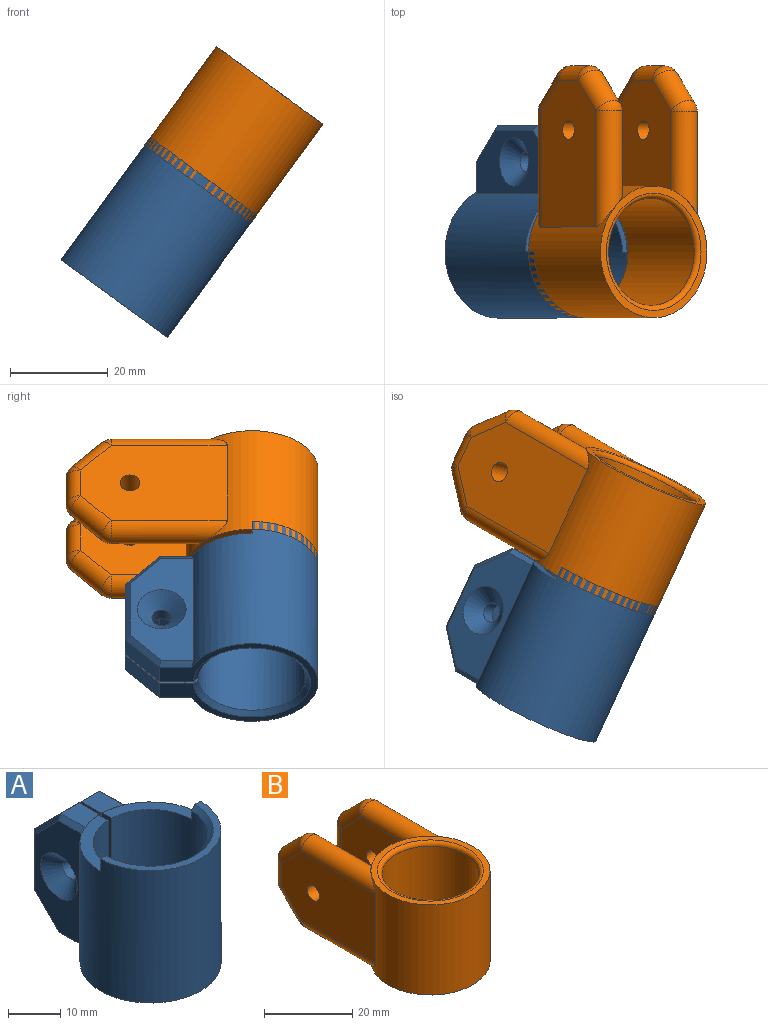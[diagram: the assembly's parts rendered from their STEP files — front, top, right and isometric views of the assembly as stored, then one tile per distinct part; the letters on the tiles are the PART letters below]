
ASSEMBLY  parts=2 mates=1
PART A: 44 faces, bbox 27x39.5x31 mm
  f0: plane 32.5x27mm, normal (0,0,-1), area 177.2mm2, adj f2,f4,f9,f12,f13,f23,f28,f33
  f1: plane 6.56x5mm, normal (0,0,1), area 29.3mm2, adj f2,f4,f14,f27,f36,f37
  f2: plane 28x12.27mm, normal (-1,0,0), area 252mm2, adj f0,f1,f11,f13,f14,f17,f18,f19
  f3: plane 26x13.03mm, normal (1,0,0), area 255.2mm2, adj f4,f17,f18,f19,f20,f21,f22,f23
  f4: cylinder r=13.5mm len=31mm, axis (0,0,-1), area 2141.3mm2, adj f0,f1,f3,f6,f8,f10,f23,f27
  f5: cylinder r=11mm len=29mm, axis (0,0,-1), area 1908.8mm2, adj f33,f34,f36,f39,f40,f41,f42,f43
  f6: plane 27x13.5mm, normal (0,0,1), area 60.1mm2, adj f4,f34,f41,f42
  f7: plane 14x5mm, normal (0,1,0), area 70mm2, adj f9,f12,f15,f30
  f8: plane 6.56x5mm, normal (0,0,1), area 29.3mm2, adj f4,f9,f15,f32,f38,f39
  f9: plane 28x12.27mm, normal (1,0,0), area 281.9mm2, adj f0,f7,f8,f12,f15,f16,f38
  f10: plane 26x13.03mm, normal (-1,0,0), area 219.1mm2, adj f4,f28,f29,f30,f31,f32,f35
  f11: plane 14x5mm, normal (0,1,0), area 70mm2, adj f2,f13,f14,f25
  f12: plane 7x7mm, normal (0,0.71,-0.71), area 49.5mm2, adj f0,f7,f9,f29
  f13: plane 7x7mm, normal (0,0.71,-0.71), area 49.5mm2, adj f0,f2,f11,f24
  f14: plane 7x7mm, normal (0,0.71,0.71), area 49.5mm2, adj f1,f2,f11,f26
  f15: plane 7x7mm, normal (0,0.71,0.71), area 49.5mm2, adj f7,f8,f9,f31
  f16: cylinder r=2mm len=4mm, axis (1,0,0), area 37.7mm2, adj f9,f35
  f17: plane 6x4.01mm, normal (0,-0.99,0.13), area 24.2mm2, adj f2,f3,f18,f22
  f18: plane 6x3.73mm, normal (0,-0.39,0.92), area 24.2mm2, adj f2,f3,f17,f19
  f19: plane 6x3.22mm, normal (0,0.61,0.8), area 24.2mm2, adj f2,f3,f18,f20
  f20: plane 6x4.01mm, normal (0,0.99,-0.13), area 24.2mm2, adj f2,f3,f19,f21
  f21: plane 6x3.73mm, normal (0,0.39,-0.92), area 24.2mm2, adj f2,f3,f20,f22
  f22: plane 6x3.22mm, normal (0,-0.61,-0.8), area 24.2mm2, adj f2,f3,f17,f21
  f23: plane 7.04x1.01mm, normal (0.71,0,-0.71), area 9.3mm2, adj f0,f3,f4,f24
  f24: plane 7.41x7.41mm, normal (0.71,0.5,-0.5), area 13.4mm2, adj f3,f13,f23,f25
  f25: plane 14x1mm, normal (0.71,0.71,0), area 19.2mm2, adj f3,f11,f24,f26
  f26: plane 7.41x7.41mm, normal (0.71,0.5,0.5), area 13.4mm2, adj f3,f14,f25,f27
  f27: plane 7.04x1.01mm, normal (0.71,0,0.71), area 9.3mm2, adj f1,f3,f4,f26
  f28: plane 7.04x1.01mm, normal (-0.71,0,-0.71), area 9.3mm2, adj f0,f4,f10,f29
  f29: plane 7.41x7.41mm, normal (-0.71,0.5,-0.5), area 13.4mm2, adj f10,f12,f28,f30
  f30: plane 14x1mm, normal (-0.71,0.71,0), area 19.2mm2, adj f7,f10,f29,f31
  f31: plane 7.41x7.41mm, normal (-0.71,0.5,0.5), area 13.4mm2, adj f10,f15,f30,f32
  f32: plane 7.04x1.01mm, normal (-0.71,0,0.71), area 9.3mm2, adj f4,f8,f10,f31
  f33: cone r=12mm half-angle=45deg, axis (0,0,-1), area 100.8mm2, adj f0,f5,f36,f39
  f34: cone r=11mm half-angle=45deg, axis (0,0,1), area 51.1mm2, adj f5,f6,f41,f42
  f35: cone r=5mm half-angle=45deg, axis (-1,0,0), area 93.3mm2, adj f10,f16
  f36: plane 28.02x2.75mm, normal (-1,0,0), area 76.4mm2, adj f0,f1,f4,f5,f33,f37,f43
  f37: plane 28x0.25mm, normal (0,-1,0), area 6.9mm2, adj f0,f1,f2,f36
  f38: plane 28x0.25mm, normal (0,-1,0), area 7.1mm2, adj f0,f8,f9,f39
  f39: plane 28.02x2.75mm, normal (1,0,0), area 76.4mm2, adj f0,f4,f5,f8,f33,f38,f40
  f40: plane 13.49x13mm, normal (0,0,1), area 46.8mm2, adj f4,f5,f39,f41
  f41: plane 2.98x2.5mm, normal (0,1,0), area 7mm2, adj f4,f5,f6,f34,f40
  f42: plane 2.98x2.5mm, normal (0,1,0), area 7mm2, adj f4,f5,f6,f34,f43
  f43: plane 13.49x13mm, normal (0,0,1), area 46.9mm2, adj f4,f5,f36,f42
PART B: 31 faces, bbox 27.5x51.9x25 mm
  f0: plane 23.27x19mm, normal (-1,0,0), area 390.5mm2, adj f1,f9,f20,f22,f24,f26,f27
  f1: cylinder r=13.5mm len=25mm, axis (0,0,-1), area 348.2mm2, adj f0,f2,f7,f8,f11,f18,f20,f27
  f2: plane 23.27x19mm, normal (1,0,0), area 390.5mm2, adj f1,f10,f11,f13,f15,f17,f18
  f3: plane 30x19mm, normal (-1,0,0), area 518.5mm2, adj f4,f10,f11,f13,f15,f17,f18
  f4: cylinder r=13.5mm len=27mm, axis (0,0,-1), area 1338.4mm2, adj f3,f5,f7,f8,f11,f18,f20,f27
  f5: plane 30x19mm, normal (1,0,0), area 518.5mm2, adj f4,f9,f20,f22,f24,f26,f27
  f6: cylinder r=11mm len=23mm, axis (0,0,-1), area 1589.6mm2, adj f29,f30
  f7: plane 27x27mm, normal (0,0,1), area 120.2mm2, adj f1,f4,f30
  f8: plane 27x27mm, normal (0,0,-1), area 120.2mm2, adj f1,f4,f29
  f9: cylinder r=2mm len=6mm, axis (1,0,0), area 75.4mm2, adj f0,f5
  f10: cylinder r=2mm len=6mm, axis (1,0,0), area 75.4mm2, adj f2,f3
  f11: cylinder r=3mm len=23.76mm, axis (0,1,0), area 186.6mm2, adj f1,f2,f3,f4,f12
  f12: sphere r=3mm, area 14.1mm2, adj f11,f13
  f13: cylinder r=3mm len=8.36mm, axis (0,0.71,0.71), area 83.2mm2, adj f2,f3,f12,f14
  f14: sphere r=3mm, area 14.1mm2, adj f13,f15
  f15: cylinder r=3mm len=6.51mm, axis (0,0,-1), area 61.4mm2, adj f2,f3,f14,f16
  f16: sphere r=3mm, area 14.1mm2, adj f15,f17
  f17: cylinder r=3mm len=8.36mm, axis (0,0.71,-0.71), area 83.2mm2, adj f2,f3,f16,f19
  f18: cylinder r=3mm len=23.76mm, axis (0,-1,0), area 186.6mm2, adj f1,f2,f3,f4,f19
  f19: sphere r=3mm, area 14.1mm2, adj f17,f18
  f20: cylinder r=3mm len=23.76mm, axis (0,1,0), area 186.6mm2, adj f0,f1,f4,f5,f21
  f21: sphere r=3mm, area 14.1mm2, adj f20,f22
  f22: cylinder r=3mm len=8.36mm, axis (0,0.71,0.71), area 83.2mm2, adj f0,f5,f21,f23
  f23: sphere r=3mm, area 14.1mm2, adj f22,f24
  f24: cylinder r=3mm len=6.51mm, axis (0,0,-1), area 61.4mm2, adj f0,f5,f23,f25
  f25: sphere r=3mm, area 14.1mm2, adj f24,f26
  f26: cylinder r=3mm len=8.36mm, axis (0,0.71,-0.71), area 83.2mm2, adj f0,f5,f25,f28
  f27: cylinder r=3mm len=23.76mm, axis (0,-1,0), area 186.6mm2, adj f0,f1,f4,f5,f28
  f28: sphere r=3mm, area 14.1mm2, adj f26,f27
  f29: torus R=12mm, axis (0,0,1), area 112.2mm2, adj f6,f8
  f30: torus R=12mm, axis (0,0,1), area 112.2mm2, adj f6,f7
PLACE A rot(axis=(0,1,0),36.1deg) t=(32.96,86.47,125.29)mm
PLACE B rot(axis=(0,1,0),36.1deg) t=(50.06,86.47,148.71)mm
MATE fastened A.f5 <-> B.f6  axis (-0.59,0,-0.81) through (50.65,86.47,149.52)mm
